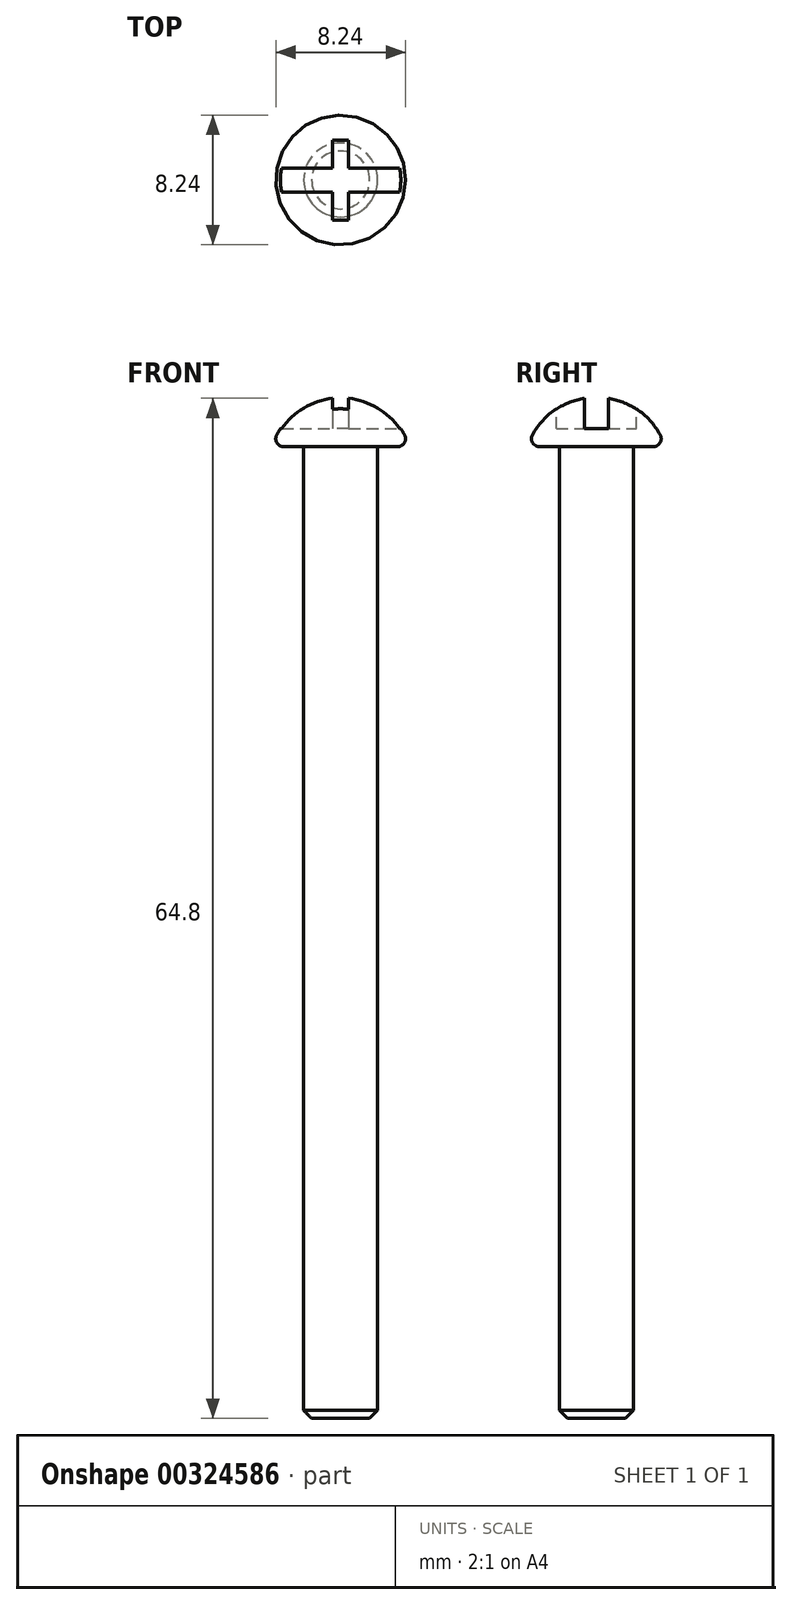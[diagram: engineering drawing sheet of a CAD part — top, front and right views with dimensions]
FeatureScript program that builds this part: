
annotation { "Feature Type Name" : "Feature", "Feature Type Description" : "" }
export const myFeature = defineFeature(function(context is Context, id is Id, definition is map)
    precondition{}
    {
        {
            var Q0;
            Q0=qCreatedBy(makeId("Front.planeOp"),FACE);
            var sketch = newSketch(context, id + "F0", { "sketchPlane" : qUnion([Q0])});
            skLineSegment(sketch, "E0", {"start": v(0, 3.18) * mm, "end": v(0, 0) * mm});
            skLineSegment(sketch, "E1", {"start": v(0, 0) * mm, "end": v(4.38, 0) * mm});
            skLineSegment(sketch, "E2", {"start": v(0, 0) * mm, "end": v(-4.38, 0) * mm, "construction": true});
            skArc(sketch, "E3", {"start": v(4.38, 0) * mm, "mid": v(2.7, 2.3) * mm, "end": v(0, 3.18) * mm});
            skPoint(sketch, "E4", {"position": v(0, 3.18) * mm});
            skPoint(sketch, "E5", {"position": v(4.38, 0) * mm});
            skSolve(sketch);
        }
        {
            var Q0;
            Q0=makeQuery(id+"F0.imprint","IMPRINT",FACE,{"disambiguationData":[TD([[makeQuery(id+"F0.imprint","IMPRINT",EDGE,{"derivedFrom":sQuery(id+"F0.wireOp",EDGE,"E0")}),1.0]])]});
            var Q1;
            Q1=sQuery(id+"F0.wireOp",EDGE,"E0");
            revolve(context, id + "F1", {"entities" : qUnion([Q0]), "axis" : qUnion([Q1]), "revolveType" : RevolveType.FULL});
        }
        {
            var Q0;
            Q0=makeQuery(id+"F1.opRevolve","SWEPT_EDGE",EDGE,{"disambiguationData":[OSD([sQuery(id+"F0.wireOp",EDGE,"E1"),sQuery(id+"F0.wireOp",EDGE,"E3")])]});
            fillet(context, id + "F2", {"entities" : qUnion([Q0]), "radius" : 0.5 * mm, "tangentPropagation" : true, "allowEdgeOverflow" : false});
        }
        {
            var Q0;
            Q0=qCreatedBy(makeId("Top.planeOp"),FACE);
            var Q1;
            Q1=sQuery(id+"F0.wireOp",VERTEX,"E4");
            cPlane(context, id + "F3", {"entities" : qUnion([Q0, Q1]), "cplaneType" : CPlaneType.PLANE_POINT, "offset" : 25.4 * mm, "width" : 152.4 * mm, "height" : 152.4 * mm});
        }
        {
            var Q0;
            Q0=qCreatedBy(id+"F3.planeOp",FACE);
            var sketch = newSketch(context, id + "F4", { "sketchPlane" : qUnion([Q0])});
            skLineSegment(sketch, "E6.bottom", {"start": v(-4.38, 0.76) * mm, "end": v(4.38, 0.76) * mm});
            skLineSegment(sketch, "E6.top", {"start": v(-4.38, -0.76) * mm, "end": v(4.38, -0.76) * mm});
            skLineSegment(sketch, "E6.left", {"start": v(-4.38, 0.76) * mm, "end": v(-4.38, -0.76) * mm});
            skLineSegment(sketch, "E6.right", {"start": v(4.38, 0.76) * mm, "end": v(4.38, -0.76) * mm});
            skPoint(sketch, "E7", {"position": v(4.38, 0) * mm});
            skPoint(sketch, "E8", {"position": v(0, 0.76) * mm});
            skSolve(sketch);
        }
        {
            var Q0;
            Q0=makeQuery(id+"F4.imprint","IMPRINT",FACE,{"disambiguationData":[TD([[makeQuery(id+"F4.imprint","IMPRINT",EDGE,{"derivedFrom":sQuery(id+"F4.wireOp",EDGE,"E6.bottom")}),-1.0]])]});
            extrude(context, id + "F5", {"entities" : qUnion([Q0]), "operationType" : NewBodyOperationType.REMOVE, "oppositeDirection" : true, "depth" : 2.03 * mm});
        }
        {
            var Q0;
            Q0=qCreatedBy(id+"F3.planeOp",FACE);
            var sketch = newSketch(context, id + "F6", { "sketchPlane" : qUnion([Q0])});
            skLineSegment(sketch, "E9.bottom", {"start": v(-0.5, 2.54) * mm, "end": v(0.5, 2.54) * mm});
            skLineSegment(sketch, "E9.top", {"start": v(-0.5, -2.54) * mm, "end": v(0.5, -2.54) * mm});
            skLineSegment(sketch, "E9.left", {"start": v(-0.5, 2.54) * mm, "end": v(-0.5, -2.54) * mm});
            skLineSegment(sketch, "E9.right", {"start": v(0.5, 2.54) * mm, "end": v(0.5, -2.54) * mm});
            skPoint(sketch, "E10", {"position": v(0, 2.54) * mm});
            skPoint(sketch, "E11", {"position": v(0.5, 0) * mm});
            skSolve(sketch);
        }
        {
            var Q0;
            Q0=makeQuery(id+"F6.imprint","IMPRINT",FACE,{"disambiguationData":[TD([[makeQuery(id+"F6.imprint","IMPRINT",EDGE,{"derivedFrom":sQuery(id+"F6.wireOp",EDGE,"E9.bottom")}),-1.0]])]});
            var Q1;
            Q1=makeQuery(id+"F5.boolean.opBoolean","COPY",FACE,{"derivedFrom":makeQuery(id+"F5.opExtrude","CAP_FACE",FACE,{"disambiguationData":[OSD([sQuery(id+"F4.wireOp",EDGE,"E6.bottom"),sQuery(id+"F4.wireOp",EDGE,"E6.top"),sQuery(id+"F4.wireOp",EDGE,"E6.left"),sQuery(id+"F4.wireOp",EDGE,"E6.right")])],"isStart":false})});
            extrude(context, id + "F7", {"entities" : qUnion([Q0]), "operationType" : NewBodyOperationType.REMOVE, "endBound" : BoundingType.UP_TO_SURFACE, "oppositeDirection" : true, "endBoundEntityFace" : qUnion([Q1]), "depth" : 25.4 * mm});
        }
        {
            var Q0;
            Q0=makeQuery(id+"F1.opRevolve","SWEPT_FACE",FACE,{"disambiguationData":[OSD([sQuery(id+"F0.wireOp",EDGE,"E1")])]});
            var sketch = newSketch(context, id + "F8", { "sketchPlane" : qUnion([Q0])});
            skCircle(sketch, "E12", {"center": v(0, 0) * mm, "radius": 2.35 * mm});
            skSolve(sketch);
        }
        {
            var Q0;
            Q0=makeQuery(id+"F8.imprint","IMPRINT",FACE,{"disambiguationData":[TD([[makeQuery(id+"F8.imprint","IMPRINT",EDGE,{"derivedFrom":sQuery(id+"F8.wireOp",EDGE,"E12")}),1.0]])]});
            extrude(context, id + "F9", {"entities" : qUnion([Q0]), "operationType" : NewBodyOperationType.ADD, "depth" : 61.72 * mm});
        }
        {
            var Q0;
            Q0=makeQuery(id+"F9.opExtrude","CAP_EDGE",EDGE,{"disambiguationData":[OSD([sQuery(id+"F8.wireOp",EDGE,"E12")])],"isStart":false});
            chamfer(context, id + "F10", {"entities" : qUnion([Q0]), "width" : 0.5 * mm, "tangentPropagation" : true});
        }
    });
